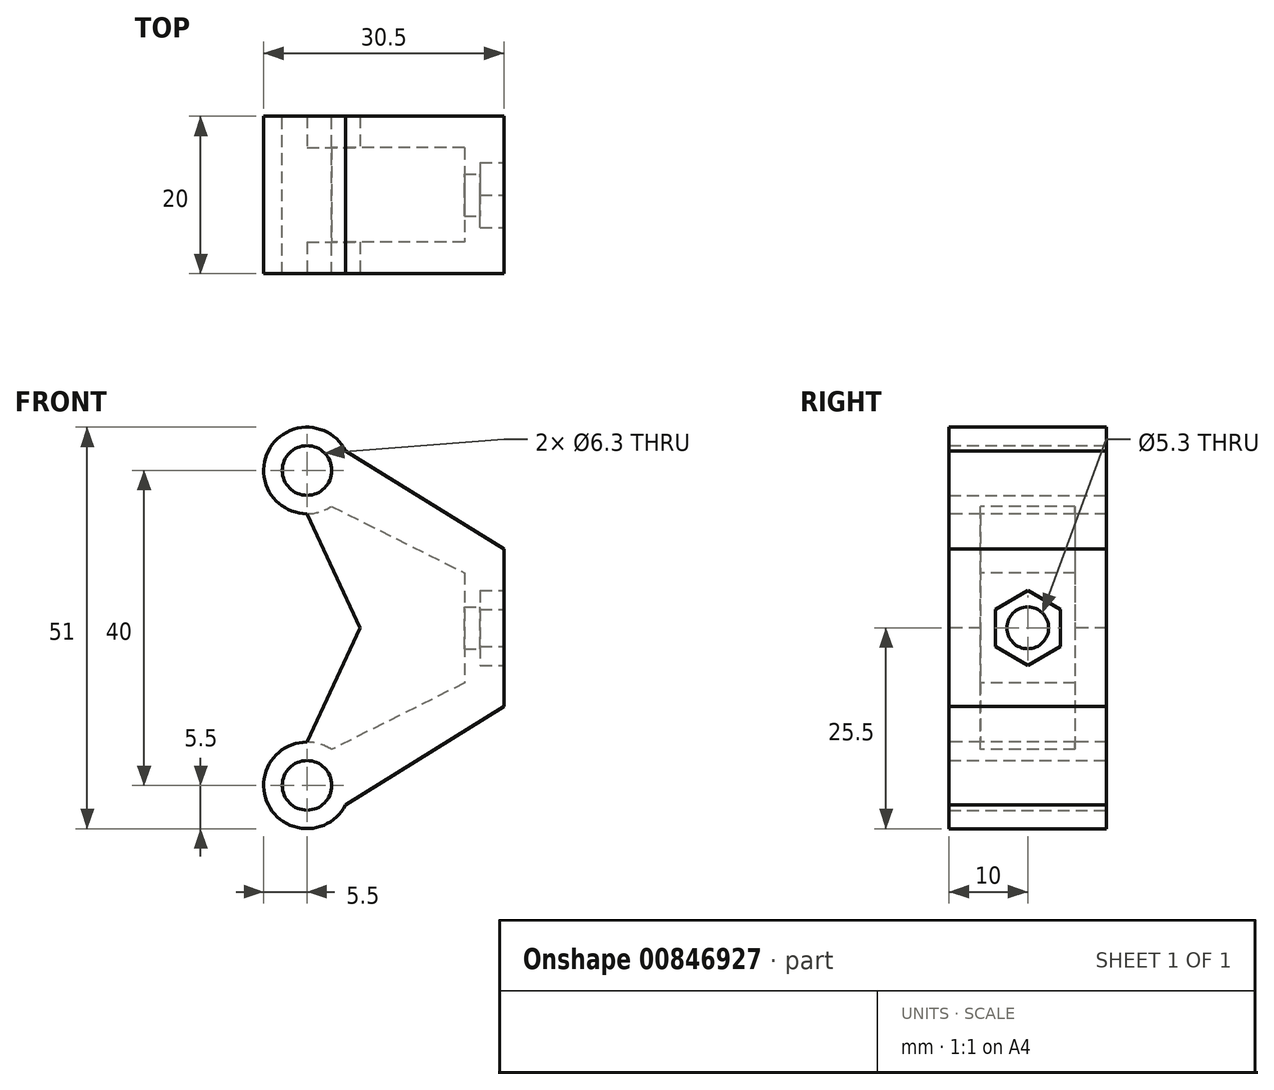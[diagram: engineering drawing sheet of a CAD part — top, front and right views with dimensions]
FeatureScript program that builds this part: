
annotation { "Feature Type Name" : "Feature", "Feature Type Description" : "" }
export const myFeature = defineFeature(function(context is Context, id is Id, definition is map)
    precondition{}
    {
        {
            var Q0;
            Q0=qCreatedBy(makeId("Front.planeOp"),FACE);
            var sketch = newSketch(context, id + "F0", { "sketchPlane" : qUnion([Q0])});
            skLineSegment(sketch, "E0", {"start": v(-10, -20) * mm, "end": v(10, -10) * mm});
            skLineSegment(sketch, "E1", {"start": v(10, -10) * mm, "end": v(10, 10) * mm});
            skLineSegment(sketch, "E2", {"start": v(10, 10) * mm, "end": v(-10, 20) * mm});
            skLineSegment(sketch, "E3", {"start": v(-10, 20) * mm, "end": v(-10, -20) * mm});
            skLineSegment(sketch, "E4", {"start": v(-10, -20) * mm, "end": v(10, 10) * mm, "construction": true});
            skLineSegment(sketch, "E5", {"start": v(-10, 20) * mm, "end": v(10, -10) * mm, "construction": true});
            skLineSegment(sketch, "E6", {"start": v(3.33, 0) * mm, "end": v(-10, 0) * mm, "construction": true});
            skLineSegment(sketch, "E7", {"start": v(10, 10) * mm, "end": v(-10, 10) * mm, "construction": true});
            skLineSegment(sketch, "E8", {"start": v(0, 0) * mm, "end": v(0, 10) * mm, "construction": true});
            skSolve(sketch);
        }
        {
            var Q0;
            Q0 = qSketchRegion(id + "F0", true);
            extrude(context, id + "F1", {"entities" : qUnion([Q0]), "endBound" : BoundingType.SYMMETRIC, "depth" : 20 * mm, "offsetDistance" : 25 * mm});
        }
        {
            var Q0;
            Q0=makeQuery(id+"F1.opExtrude","CAP_FACE",FACE,{"disambiguationData":[OSD([sQuery(id+"F0.wireOp",EDGE,"E0"),sQuery(id+"F0.wireOp",EDGE,"E1"),sQuery(id+"F0.wireOp",EDGE,"E2"),sQuery(id+"F0.wireOp",EDGE,"E3")])],"isStart":false});
            var sketch = newSketch(context, id + "F2", { "sketchPlane" : qUnion([Q0])});
            skLineSegment(sketch, "E9", {"start": v(10, -10) * mm, "end": v(15, -10) * mm});
            skLineSegment(sketch, "E10", {"start": v(15, -10) * mm, "end": v(15, 10) * mm});
            skLineSegment(sketch, "E11", {"start": v(15, 10) * mm, "end": v(10, 10) * mm});
            skLineSegment(sketch, "E12.0", {"start": v(10, -10) * mm, "end": v(10, 10) * mm});
            skSolve(sketch);
        }
        {
            var Q0;
            Q0 = qSketchRegion(id + "F2", true);
            var Q1;
            Q1=makeQuery(id+"F1.opExtrude","CAP_FACE",FACE,{"disambiguationData":[OSD([sQuery(id+"F0.wireOp",EDGE,"E0"),sQuery(id+"F0.wireOp",EDGE,"E1"),sQuery(id+"F0.wireOp",EDGE,"E2"),sQuery(id+"F0.wireOp",EDGE,"E3")])],"isStart":true});
            extrude(context, id + "F3", {"entities" : qUnion([Q0]), "operationType" : NewBodyOperationType.ADD, "endBound" : BoundingType.UP_TO_SURFACE, "oppositeDirection" : true, "depth" : 25 * mm, "endBoundEntityFace" : qUnion([Q1]), "offsetDistance" : 25 * mm});
        }
        {
            var Q0;
            Q0=makeQuery(id+"F3.opExtrude","SWEPT_FACE",FACE,{"disambiguationData":[OSD([sQuery(id+"F2.wireOp",EDGE,"E10")])]});
            var sketch = newSketch(context, id + "F4", { "sketchPlane" : qUnion([Q0])});
            skCircle(sketch, "E13.cCircle", {"center": v(0, 0) * mm, "radius": 4.11 * mm, "construction": true});
            skLineSegment(sketch, "E13.0", {"start": v(4.11, -2.37) * mm, "end": v(0, -4.75) * mm});
            skLineSegment(sketch, "E13.1", {"start": v(0, -4.75) * mm, "end": v(-4.11, -2.38) * mm});
            skLineSegment(sketch, "E13.2", {"start": v(-4.11, -2.38) * mm, "end": v(-4.11, 2.37) * mm});
            skLineSegment(sketch, "E13.3", {"start": v(-4.11, 2.37) * mm, "end": v(0, 4.75) * mm});
            skLineSegment(sketch, "E13.4", {"start": v(0, 4.75) * mm, "end": v(4.11, 2.38) * mm});
            skLineSegment(sketch, "E13.5", {"start": v(4.11, 2.38) * mm, "end": v(4.11, -2.37) * mm});
            skPoint(sketch, "E13.0.midPoint", {"position": v(2.06, -3.56) * mm});
            skLineSegment(sketch, "E14", {"start": v(-10, -10) * mm, "end": v(10, 10) * mm, "construction": true});
            skLineSegment(sketch, "E15", {"start": v(-10, 10) * mm, "end": v(10, -10) * mm, "construction": true});
            skSolve(sketch);
        }
        {
            var Q0;
            Q0 = qSketchRegion(id + "F4", true);
            extrude(context, id + "F5", {"entities" : qUnion([Q0]), "operationType" : NewBodyOperationType.REMOVE, "oppositeDirection" : true, "depth" : 3 * mm, "offsetDistance" : 25 * mm});
        }
        {
            var Q0;
            Q0=makeQuery(id+"F3.boolean.opBoolean","MERGE",FACE,{"derivedFrom":[makeQuery(id+"F1.opExtrude","CAP_FACE",FACE,{"disambiguationData":[OSD([sQuery(id+"F0.wireOp",EDGE,"E0"),sQuery(id+"F0.wireOp",EDGE,"E1"),sQuery(id+"F0.wireOp",EDGE,"E2"),sQuery(id+"F0.wireOp",EDGE,"E3")])],"isStart":false}),makeQuery(id+"F3.opExtrude","CAP_FACE",FACE,{"disambiguationData":[OSD([sQuery(id+"F2.wireOp",EDGE,"E9"),sQuery(id+"F2.wireOp",EDGE,"E10"),sQuery(id+"F2.wireOp",EDGE,"E11"),sQuery(id+"F2.wireOp",EDGE,"E12.0")])],"isStart":true})]});
            cPlane(context, id + "F6", {"entities" : qUnion([Q0]), "cplaneType" : CPlaneType.OFFSET, "offset" : 4 * mm, "oppositeDirection" : true, "width" : 150 * mm, "height" : 150 * mm});
        }
        {
            var Q0;
            Q0=qCreatedBy(id+"F6.planeOp",FACE);
            var sketch = newSketch(context, id + "F7", { "sketchPlane" : qUnion([Q0])});
            skLineSegment(sketch, "E16", {"start": v(-10, -17) * mm, "end": v(10, -7) * mm});
            skLineSegment(sketch, "E17", {"start": v(10, -7) * mm, "end": v(10, 7) * mm});
            skLineSegment(sketch, "E18", {"start": v(10, 7) * mm, "end": v(-10, 17) * mm});
            skLineSegment(sketch, "E19", {"start": v(-10, 17) * mm, "end": v(-10, -17) * mm});
            skSolve(sketch);
        }
        {
            var Q0;
            Q0 = qSketchRegion(id + "F7", true);
            var Q1;
            {var subQ0=sQuery(id+"F0.wireOp",EDGE,"E3");var subQ1=sQuery(id+"F0.wireOp",EDGE,"E2");var subQ2=sQuery(id+"F0.wireOp",EDGE,"E1");var subQ3=sQuery(id+"F0.wireOp",EDGE,"E0");Q1=makeQuery(id+"F3.boolean.opBoolean","MERGE",FACE,{"derivedFrom":[makeQuery(id+"F1.opExtrude","CAP_FACE",FACE,{"disambiguationData":[OSD([subQ3,subQ2,subQ1,subQ0])],"isStart":true}),makeQuery(id+"F3.opExtrude","CAP_FACE",FACE,{"disambiguationData":[OSD([subQ3,subQ2,subQ1,subQ0])],"isStart":false})]});}
            extrude(context, id + "F8", {"entities" : qUnion([Q0]), "operationType" : NewBodyOperationType.REMOVE, "endBound" : BoundingType.UP_TO_SURFACE, "oppositeDirection" : true, "depth" : 25 * mm, "endBoundEntityFace" : qUnion([Q1]), "hasOffset" : true, "offsetDistance" : 4 * mm});
        }
        {
            var Q0;
            Q0=makeQuery(id+"F3.boolean.opBoolean","MERGE",FACE,{"derivedFrom":[makeQuery(id+"F1.opExtrude","CAP_FACE",FACE,{"disambiguationData":[OSD([sQuery(id+"F0.wireOp",EDGE,"E0"),sQuery(id+"F0.wireOp",EDGE,"E1"),sQuery(id+"F0.wireOp",EDGE,"E2"),sQuery(id+"F0.wireOp",EDGE,"E3")])],"isStart":false}),makeQuery(id+"F3.opExtrude","CAP_FACE",FACE,{"disambiguationData":[OSD([sQuery(id+"F2.wireOp",EDGE,"E9"),sQuery(id+"F2.wireOp",EDGE,"E10"),sQuery(id+"F2.wireOp",EDGE,"E11"),sQuery(id+"F2.wireOp",EDGE,"E12.0")])],"isStart":true})]});
            var sketch = newSketch(context, id + "F9", { "sketchPlane" : qUnion([Q0])});
            skCircle(sketch, "E20", {"center": v(-10, 20) * mm, "radius": 5.5 * mm});
            skCircle(sketch, "E21", {"center": v(-10, -20) * mm, "radius": 5.5 * mm});
            skSolve(sketch);
        }
        {
            var Q0;
            Q0 = qSketchRegion(id + "F9", true);
            var Q1;
            {var subQ0=sQuery(id+"F0.wireOp",EDGE,"E3");var subQ1=sQuery(id+"F0.wireOp",EDGE,"E2");var subQ2=sQuery(id+"F0.wireOp",EDGE,"E1");var subQ3=sQuery(id+"F0.wireOp",EDGE,"E0");Q1=makeQuery(id+"F3.boolean.opBoolean","MERGE",FACE,{"derivedFrom":[makeQuery(id+"F1.opExtrude","CAP_FACE",FACE,{"disambiguationData":[OSD([subQ3,subQ2,subQ1,subQ0])],"isStart":true}),makeQuery(id+"F3.opExtrude","CAP_FACE",FACE,{"disambiguationData":[OSD([subQ3,subQ2,subQ1,subQ0])],"isStart":false})]});}
            extrude(context, id + "F10", {"entities" : qUnion([Q0]), "operationType" : NewBodyOperationType.ADD, "endBound" : BoundingType.UP_TO_SURFACE, "oppositeDirection" : true, "depth" : 25 * mm, "endBoundEntityFace" : qUnion([Q1]), "offsetDistance" : 25 * mm});
        }
        {
            var Q0;
            Q0=makeQuery(id+"F5.boolean.opBoolean","COPY",FACE,{"derivedFrom":makeQuery(id+"F5.opExtrude","CAP_FACE",FACE,{"disambiguationData":[OSD([sQuery(id+"F4.wireOp",EDGE,"E13.0"),sQuery(id+"F4.wireOp",EDGE,"E13.1"),sQuery(id+"F4.wireOp",EDGE,"E13.2"),sQuery(id+"F4.wireOp",EDGE,"E13.3"),sQuery(id+"F4.wireOp",EDGE,"E13.4"),sQuery(id+"F4.wireOp",EDGE,"E13.5")])],"isStart":false})});
            var sketch = newSketch(context, id + "F11", { "sketchPlane" : qUnion([Q0])});
            skCircle(sketch, "E22", {"center": v(0, 0) * mm, "radius": 2.65 * mm});
            skSolve(sketch);
        }
        {
            var Q0;
            Q0 = qSketchRegion(id + "F11", true);
            extrude(context, id + "F12", {"entities" : qUnion([Q0]), "operationType" : NewBodyOperationType.REMOVE, "oppositeDirection" : true, "depth" : 25 * mm, "offsetDistance" : 25 * mm});
        }
        {
            var Q0;
            {var subQ0=sQuery(id+"F0.wireOp",EDGE,"E3");var subQ1=sQuery(id+"F0.wireOp",EDGE,"E2");var subQ2=sQuery(id+"F0.wireOp",EDGE,"E1");var subQ3=sQuery(id+"F0.wireOp",EDGE,"E0");Q0=makeQuery(id+"F10.boolean.opBoolean","MERGE",FACE,{"derivedFrom":[makeQuery(id+"F3.boolean.opBoolean","MERGE",FACE,{"derivedFrom":[makeQuery(id+"F1.opExtrude","CAP_FACE",FACE,{"disambiguationData":[OSD([subQ3,subQ2,subQ1,subQ0])],"isStart":true}),makeQuery(id+"F3.opExtrude","CAP_FACE",FACE,{"disambiguationData":[OSD([subQ3,subQ2,subQ1,subQ0])],"isStart":false})]}),makeQuery(id+"F10.opExtrude","CAP_FACE",FACE,{"disambiguationData":[OSD([subQ3,subQ2,subQ1,subQ0]),OD(0.0)],"isStart":false}),makeQuery(id+"F10.opExtrude","CAP_FACE",FACE,{"disambiguationData":[OSD([subQ3,subQ2,subQ1,subQ0]),OD(1.0)],"isStart":false})]});}
            var sketch = newSketch(context, id + "F13", { "sketchPlane" : qUnion([Q0])});
            skArc(sketch, "E23.0", {"start": v(5.08, -17.54) * mm, "mid": v(12.9, -24.68) * mm, "end": v(10, -14.5) * mm, "construction": true});
            skArc(sketch, "E24.0", {"start": v(10, 14.5) * mm, "mid": v(12.9, 24.68) * mm, "end": v(5.08, 17.54) * mm, "construction": true});
            skCircle(sketch, "E25", {"center": v(10, -20) * mm, "radius": 3.15 * mm});
            skCircle(sketch, "E26", {"center": v(10, 20) * mm, "radius": 3.15 * mm});
            skSolve(sketch);
        }
        {
            var Q0;
            Q0 = qSketchRegion(id + "F13", true);
            extrude(context, id + "F14", {"entities" : qUnion([Q0]), "operationType" : NewBodyOperationType.REMOVE, "oppositeDirection" : true, "depth" : 25 * mm, "offsetDistance" : 25 * mm});
        }
        {
            var Q0;
            {var subQ0=sQuery(id+"F0.wireOp",EDGE,"E3");var subQ1=sQuery(id+"F0.wireOp",EDGE,"E2");var subQ2=sQuery(id+"F0.wireOp",EDGE,"E1");var subQ3=sQuery(id+"F0.wireOp",EDGE,"E0");Q0=makeQuery(id+"F10.boolean.opBoolean","MERGE",FACE,{"derivedFrom":[makeQuery(id+"F3.boolean.opBoolean","MERGE",FACE,{"derivedFrom":[makeQuery(id+"F1.opExtrude","CAP_FACE",FACE,{"disambiguationData":[OSD([subQ3,subQ2,subQ1,subQ0])],"isStart":true}),makeQuery(id+"F3.opExtrude","CAP_FACE",FACE,{"disambiguationData":[OSD([subQ3,subQ2,subQ1,subQ0])],"isStart":false})]}),makeQuery(id+"F10.opExtrude","CAP_FACE",FACE,{"disambiguationData":[OSD([subQ3,subQ2,subQ1,subQ0]),OD(0.0)],"isStart":false}),makeQuery(id+"F10.opExtrude","CAP_FACE",FACE,{"disambiguationData":[OSD([subQ3,subQ2,subQ1,subQ0]),OD(1.0)],"isStart":false})]});}
            var sketch = newSketch(context, id + "F15", { "sketchPlane" : qUnion([Q0])});
            skLineSegment(sketch, "E27", {"start": v(5.08, 17.54) * mm, "end": v(5.08, 22.46) * mm});
            skLineSegment(sketch, "E28", {"start": v(5.08, -17.54) * mm, "end": v(5.08, -22.46) * mm});
            skLineSegment(sketch, "E29", {"start": v(5.08, -22.46) * mm, "end": v(-15, -10) * mm});
            skLineSegment(sketch, "E30", {"start": v(-15, -10) * mm, "end": v(-10, -10) * mm});
            skLineSegment(sketch, "E31", {"start": v(-10, -10) * mm, "end": v(5.08, -17.54) * mm});
            skLineSegment(sketch, "E32", {"start": v(5.08, 22.46) * mm, "end": v(-15, 10) * mm});
            skLineSegment(sketch, "E33", {"start": v(-15, 10) * mm, "end": v(-10, 10) * mm});
            skLineSegment(sketch, "E34", {"start": v(5.08, 17.54) * mm, "end": v(-10, 10) * mm});
            skSolve(sketch);
        }
        {
            var Q0;
            Q0 = qSketchRegion(id + "F15", true);
            var Q1;
            Q1=makeQuery(id+"F10.boolean.opBoolean","MERGE",FACE,{"derivedFrom":[makeQuery(id+"F3.boolean.opBoolean","MERGE",FACE,{"derivedFrom":[makeQuery(id+"F1.opExtrude","CAP_FACE",FACE,{"disambiguationData":[OSD([sQuery(id+"F0.wireOp",EDGE,"E0"),sQuery(id+"F0.wireOp",EDGE,"E1"),sQuery(id+"F0.wireOp",EDGE,"E2"),sQuery(id+"F0.wireOp",EDGE,"E3")])],"isStart":false}),makeQuery(id+"F3.opExtrude","CAP_FACE",FACE,{"disambiguationData":[OSD([sQuery(id+"F2.wireOp",EDGE,"E9"),sQuery(id+"F2.wireOp",EDGE,"E10"),sQuery(id+"F2.wireOp",EDGE,"E11"),sQuery(id+"F2.wireOp",EDGE,"E12.0")])],"isStart":true})]}),makeQuery(id+"F10.opExtrude","CAP_FACE",FACE,{"disambiguationData":[OSD([sQuery(id+"F9.wireOp",EDGE,"E20")])],"isStart":true}),makeQuery(id+"F10.opExtrude","CAP_FACE",FACE,{"disambiguationData":[OSD([sQuery(id+"F9.wireOp",EDGE,"E21")])],"isStart":true})]});
            extrude(context, id + "F16", {"entities" : qUnion([Q0]), "operationType" : NewBodyOperationType.ADD, "endBound" : BoundingType.UP_TO_SURFACE, "oppositeDirection" : true, "depth" : 25 * mm, "endBoundEntityFace" : qUnion([Q1]), "offsetDistance" : 25 * mm});
        }
        {
            var Q0;
            {var subQ0=sQuery(id+"F9.wireOp",EDGE,"E21");var subQ1=sQuery(id+"F9.wireOp",EDGE,"E20");var subQ2=sQuery(id+"F2.wireOp",EDGE,"E12.0");var subQ3=sQuery(id+"F2.wireOp",EDGE,"E11");var subQ4=sQuery(id+"F2.wireOp",EDGE,"E10");var subQ5=sQuery(id+"F2.wireOp",EDGE,"E9");var subQ6=sQuery(id+"F0.wireOp",EDGE,"E3");var subQ7=sQuery(id+"F0.wireOp",EDGE,"E2");var subQ8=sQuery(id+"F0.wireOp",EDGE,"E1");var subQ9=sQuery(id+"F0.wireOp",EDGE,"E0");Q0=makeQuery(id+"F16.boolean.opBoolean","MERGE",FACE,{"derivedFrom":[makeQuery(id+"F10.boolean.opBoolean","MERGE",FACE,{"derivedFrom":[makeQuery(id+"F3.boolean.opBoolean","MERGE",FACE,{"derivedFrom":[makeQuery(id+"F1.opExtrude","CAP_FACE",FACE,{"disambiguationData":[OSD([subQ9,subQ8,subQ7,subQ6])],"isStart":false}),makeQuery(id+"F3.opExtrude","CAP_FACE",FACE,{"disambiguationData":[OSD([subQ5,subQ4,subQ3,subQ2])],"isStart":true})]}),makeQuery(id+"F10.opExtrude","CAP_FACE",FACE,{"disambiguationData":[OSD([subQ1])],"isStart":true}),makeQuery(id+"F10.opExtrude","CAP_FACE",FACE,{"disambiguationData":[OSD([subQ0])],"isStart":true})]}),makeQuery(id+"F16.opExtrude","CAP_FACE",FACE,{"disambiguationData":[OSD([subQ9,subQ8,subQ7,subQ6,subQ5,subQ4,subQ3,subQ2,subQ1,subQ0]),OD(0.0)],"isStart":false}),makeQuery(id+"F16.opExtrude","CAP_FACE",FACE,{"disambiguationData":[OSD([subQ9,subQ8,subQ7,subQ6,subQ5,subQ4,subQ3,subQ2,subQ1,subQ0]),OD(1.0)],"isStart":false})]});}
            var sketch = newSketch(context, id + "F17", { "sketchPlane" : qUnion([Q0])});
            skLineSegment(sketch, "E35", {"start": v(-10, 14.5) * mm, "end": v(-3.23, 0) * mm});
            skLineSegment(sketch, "E36", {"start": v(-3.23, 0) * mm, "end": v(-10, -14.5) * mm});
            skLineSegment(sketch, "E37", {"start": v(-10, -14.5) * mm, "end": v(-10, 14.5) * mm});
            skSolve(sketch);
        }
        {
            var Q0;
            Q0 = qSketchRegion(id + "F17", true);
            extrude(context, id + "F18", {"entities" : qUnion([Q0]), "operationType" : NewBodyOperationType.REMOVE, "oppositeDirection" : true, "depth" : 25 * mm, "offsetDistance" : 25 * mm});
        }
    });
